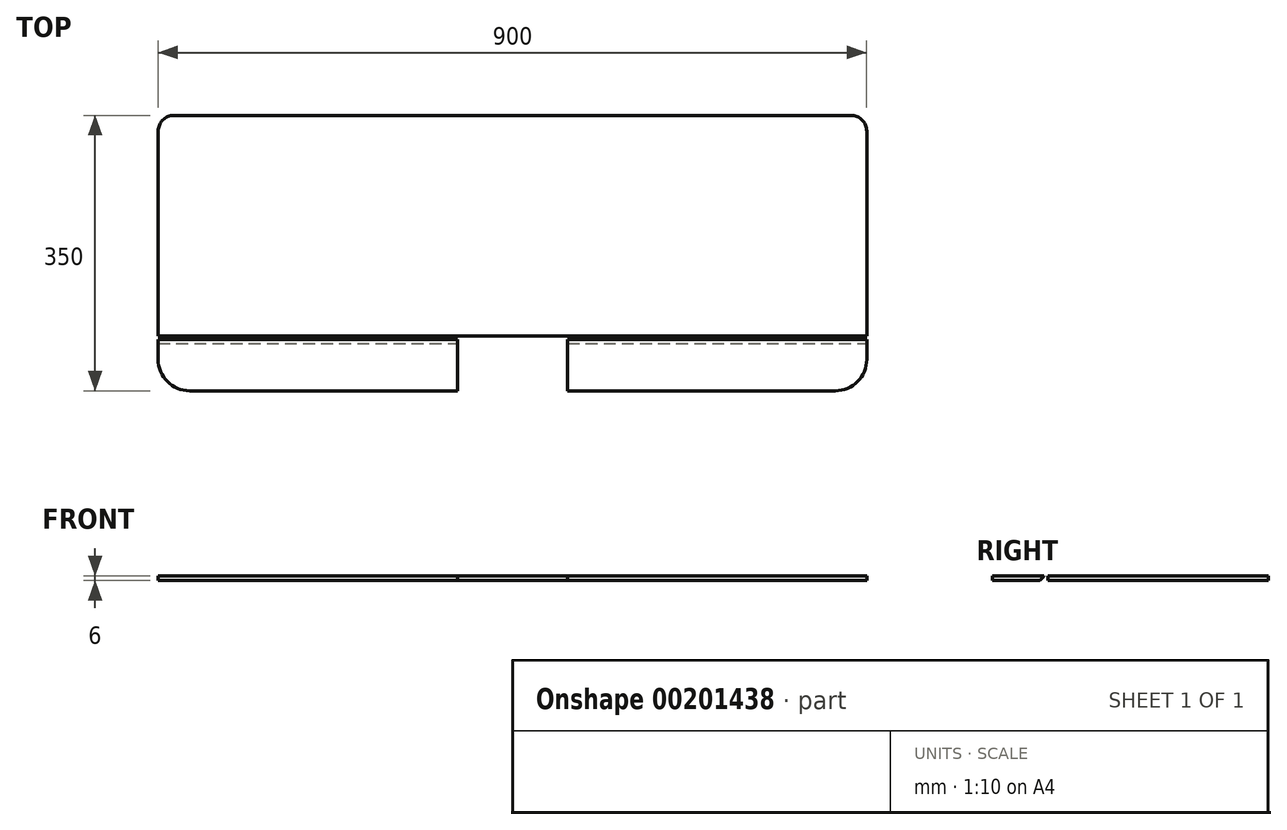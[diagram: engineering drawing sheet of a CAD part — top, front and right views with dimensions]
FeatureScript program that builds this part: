
annotation { "Feature Type Name" : "Feature", "Feature Type Description" : "" }
export const myFeature = defineFeature(function(context is Context, id is Id, definition is map)
    precondition{}
    {
        {
            var Q0;
            Q0=qCreatedBy(makeId("Top.planeOp"),FACE);
            var sketch = newSketch(context, id + "F0", { "sketchPlane" : qUnion([Q0])});
            skLineSegment(sketch, "E0", {"start": v(-335.48, 325.76) * mm, "end": v(524.52, 325.76) * mm});
            skLineSegment(sketch, "E1", {"start": v(544.52, 305.76) * mm, "end": v(544.52, 45.76) * mm});
            skLineSegment(sketch, "E2", {"start": v(544.52, 45.76) * mm, "end": v(-300.8, 45.76) * mm});
            skLineSegment(sketch, "E3", {"start": v(-355.48, 305.76) * mm, "end": v(-355.48, 45.76) * mm});
            skLineSegment(sketch, "E4", {"start": v(-300.8, 45.76) * mm, "end": v(-355.48, 45.76) * mm});
            skLineSegment(sketch, "E5", {"start": v(544.52, 40.76) * mm, "end": v(544.52, 15.76) * mm});
            skLineSegment(sketch, "E6", {"start": v(504.52, -24.24) * mm, "end": v(-315.48, -24.24) * mm});
            skLineSegment(sketch, "E7", {"start": v(-355.48, 15.76) * mm, "end": v(-355.48, 40.76) * mm});
            skLineSegment(sketch, "E8", {"start": v(-355.48, 40.76) * mm, "end": v(544.52, 40.76) * mm});
            skPoint(sketch, "E9.visualSharp", {"position": v(-355.48, 325.76) * mm});
            skArc(sketch, "E9.filletArc", {"start": v(-335.48, 325.76) * mm, "mid": v(-349.62, 319.9) * mm, "end": v(-355.48, 305.76) * mm});
            skPoint(sketch, "E10.visualSharp", {"position": v(544.52, 325.76) * mm});
            skArc(sketch, "E10.filletArc", {"start": v(544.52, 305.76) * mm, "mid": v(538.67, 319.9) * mm, "end": v(524.52, 325.76) * mm});
            skPoint(sketch, "E11.visualSharp", {"position": v(-355.48, -24.24) * mm});
            skArc(sketch, "E11.filletArc", {"start": v(-355.48, 15.76) * mm, "mid": v(-343.76, -12.53) * mm, "end": v(-315.48, -24.24) * mm});
            skPoint(sketch, "E12.visualSharp", {"position": v(544.52, -24.24) * mm});
            skArc(sketch, "E12.filletArc", {"start": v(504.52, -24.24) * mm, "mid": v(532.8, -12.53) * mm, "end": v(544.52, 15.76) * mm});
            skLineSegment(sketch, "E13", {"start": v(94.52, 325.76) * mm, "end": v(94.52, -120.83) * mm});
            skPoint(sketch, "E13.endSnap0", {"position": v(94.52, 40.76) * mm});
            skLineSegment(sketch, "E14.bottom", {"start": v(24.52, 40.76) * mm, "end": v(164.52, 40.76) * mm});
            skLineSegment(sketch, "E14.top", {"start": v(24.52, -24.24) * mm, "end": v(164.52, -24.24) * mm});
            skLineSegment(sketch, "E14.left", {"start": v(24.52, 40.76) * mm, "end": v(24.52, -24.24) * mm});
            skLineSegment(sketch, "E14.right", {"start": v(164.52, 40.76) * mm, "end": v(164.52, -24.24) * mm});
            skSolve(sketch);
        }
        {
            var Q0;
            Q0=makeQuery(id+"F0.imprint","IMPRINT",FACE,{"disambiguationData":[TD([[makeQuery(id+"F0.imprint","IMPRINT",EDGE,{"derivedFrom":sQuery(id+"F0.wireOp",EDGE,"E3")}),1.0]])]});
            var Q1;
            {var subQ2=sQuery(id+"F0.wireOp",EDGE,"E5");Q1=makeQuery(id+"F0.imprint","IMPRINT",FACE,{"disambiguationData":[TD([[makeQuery(id+"F0.imprint","IMPRINT",EDGE,{"derivedFrom":subQ2}),-1.0]])]});}
            var Q2;
            {var subQ2=sQuery(id+"F0.wireOp",EDGE,"E7");Q2=makeQuery(id+"F0.imprint","IMPRINT",FACE,{"disambiguationData":[TD([[makeQuery(id+"F0.imprint","IMPRINT",EDGE,{"derivedFrom":subQ2}),-1.0]])]});}
            var Q3;
            {var subQ2=sQuery(id+"F0.wireOp",EDGE,"E1");Q3=makeQuery(id+"F0.imprint","IMPRINT",FACE,{"disambiguationData":[TD([[makeQuery(id+"F0.imprint","IMPRINT",EDGE,{"derivedFrom":subQ2}),-1.0]])]});}
            extrude(context, id + "F1", {"entities" : qUnion([Q0, Q1, Q2, Q3]), "depth" : 6 * mm});
        }
        {
            var Q0;
            {var subQ0=sQuery(id+"F0.wireOp",EDGE,"E8");Q0=makeQuery(id+"F1.opExtrude","CAP_EDGE",EDGE,{"disambiguationData":[OSD([subQ0]),TDD([makeQuery(id+"F0.imprint","IMPRINT",EDGE,{"disambiguationData":[TD([[makeQuery(id+"F0.imprint","INTERSECT",VERTEX,{"derivedFrom":[sQuery(id+"F0.wireOp",EDGE,"E7"),subQ0]}),-1.0]])],"derivedFrom":subQ0})])],"isStart":true});}
            chamfer(context, id + "F2", {"entities" : qUnion([Q0]), "width" : 5 * mm, "tangentPropagation" : true});
        }
        {
            var Q0;
            {var subQ0=sQuery(id+"F0.wireOp",EDGE,"E8");Q0=makeQuery(id+"F1.opExtrude","CAP_EDGE",EDGE,{"disambiguationData":[OSD([subQ0]),TDD([makeQuery(id+"F0.imprint","IMPRINT",EDGE,{"disambiguationData":[TD([[makeQuery(id+"F0.imprint","INTERSECT",VERTEX,{"derivedFrom":[sQuery(id+"F0.wireOp",EDGE,"E5"),subQ0]}),1.0]])],"derivedFrom":subQ0})])],"isStart":true});}
            chamfer(context, id + "F3", {"entities" : qUnion([Q0]), "width" : 5 * mm, "tangentPropagation" : true});
        }
    });
